# Revit family: Kühltische GN1-1 - Magnos - Eigen
name_source: partatom
category: Sonderausstattung
revit_build: Autodesk Revit 2015 (Build: 20160512_1515(x64)
units: mm (PartAtom-declared; Revit-internal decimal feet)

## types (2) — shared parameters
Abstand Display seitlich = 60 mm  [stored 0.19685 ft]
Abstand Logo = 265 mm
Aufkantung Höhe = 50 mm  [stored 0.164042 ft]
Aufkantung Stärke = 6 mm  [stored 0.019685 ft]
Höhe Elektroanschluss = 150 mm
Korpus Höhe = 650 mm  [stored 2.13255 ft]
Korpus Tiefe = 620 mm
Kälteleistung = 330 Watt -10°C VT/+32°C UT
Kältemittel = R134a
Material = Edelstahl AISI 304
Pfosten 1 = Ja
Pfosten Breite = 100 mm  [stored 0.328084 ft]
Pfosten Tiefe = 50 mm  [stored 0.164042 ft]
Platte Stärke = 50 mm  [stored 0.164042 ft]
Platte Tiefe = 700 mm  [stored 2.29659 ft]
Pole = 1
Rückwand Stärke = 50 mm  [stored 0.164042 ft]
Scheinleistung = 0 VA
Seitenteil Breite = 320 mm  [stored 1.04987 ft]
Seitenteilwand Stärke = 15 mm  [stored 0.0492126 ft]
Seitenwand Stärke = 50 mm  [stored 0.164042 ft]
Sockelhöhe = 150 mm
Spannung = 230 V
Temp. Bereich = 0°C bis +10°C
Tür_1 = Ja
Tür_2 = Ja
Türen Breite = 430 mm  [stored 1.41076 ft]
Türen Breite halb = 215 mm  [stored 0.705381 ft]
Türen Höhe = 630 mm  [stored 2.06693 ft]
Türen Stärke = 50 mm  [stored 0.164042 ft]
Wand oben Stärke = 50 mm  [stored 0.164042 ft]
Wand unten Stärke = 50 mm  [stored 0.164042 ft]
Öffnungstiefe = 470 mm

## per-type parameters (varying)
| type | Artnr mit Platte | Artnr mit Platte und Aufkantung | Artnr ohne Platte | Breite | Energieverbrauch | Kapazität | Korpus Breite | Pfosten 2 | Pfosten Abstand | Pfosten Anzahl | Tür_3 | Türen Anzahl | Türen Lücke | Versatz Tür zu Seitenteil | Watt |
| 650x1250 2-türig | KTM 721162-MS | KTM 721161-MS | KTM 721160-MS | 1250 mm  [stored 4.10105 ft] | 2,7 kWh/24 h | 2 x 8 x GN1/1 | 915 mm | Nein | 440 mm | 1 | Nein | 2 | 20 mm  [stored 0.0656168 ft] | 20 mm  [stored 0.0656168 ft] | 380 W |
| 650x1725 3-türig | KTM 731162-MS | KTM 731161-MS | KTM 731160-MS | 1725 mm  [stored 5.65945 ft] | 3,2 kWh/24 h | 3 x 8 x GN1/1 | 1390 mm | Ja | 445 mm | 2 | Ja | 3 | 30 mm  [stored 0.0984252 ft] | 25 mm  [stored 0.082021 ft] | 400 W |

note: [stored X ft] marks values corroborated as IEEE doubles in the binary element streams (Revit-internal decimal feet)

## geometry (parser evidence)
native form markers: Blend x15, Sweep x3
no freeform markers — native parametric forms only
